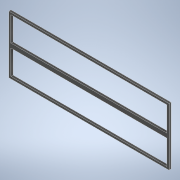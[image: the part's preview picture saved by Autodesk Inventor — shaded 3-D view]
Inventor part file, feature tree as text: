
AUTODESK INVENTOR PART (.ipt)
format: ipt  version: 2022 (Build 260153000, 153)  size: 112,640 bytes
history: native  units: mm
features: other x1, extrude x1, sketch x1
ambient origin geometry x8: Origin, YZ Plane, XZ Plane, XY Plane, X Axis, Y Axis, Z Axis, Center Point
bodies: Body1 (feature_tree)
feature tree (3):
  other  "Sólido1"
  extrude  "Extrusão1"  Depth=27.0mm
  sketch  "Esboço1"  dims[d6=150.0mm d7=27.0mm d8=2.0mm d9=2.0mm d10=2.0mm d11=2.0mm d12=2.0mm d13=0.0mm]
